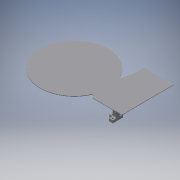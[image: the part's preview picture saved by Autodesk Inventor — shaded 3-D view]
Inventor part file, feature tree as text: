
AUTODESK INVENTOR PART (.ipt)
format: ipt  version: 2018 (Build 220112000, 112)  size: 204,800 bytes
history: native  units: mm
features: sketch x6, other x3
ambient origin geometry x8: Origin, YZ Plane, XZ Plane, XY Plane, X Axis, Y Axis, Z Axis, Center Point
bodies: Volumenkörper1 (feature_tree)
feature tree (9):
  other  "SolarpanelHalterung_MIR.ipt"
  other  "Volumenkörper1::SolarpanelHalterung_MIR.ipt"
  other  "Bezeichnung1"
  sketch  "Skizze1"  dims[d0=10.0mm]
  sketch  "Skizze2"
  sketch  "Skizze3"
  sketch  "Skizze4"
  sketch  "Skizze5"
  sketch  "Skizze6"
